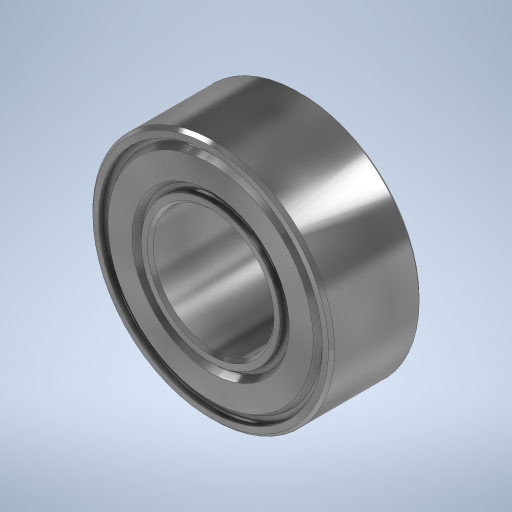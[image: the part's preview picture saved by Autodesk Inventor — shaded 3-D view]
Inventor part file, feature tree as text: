
AUTODESK INVENTOR PART (.ipt)
format: ipt  version: 2023.1 (Build 271208000, 208)  size: 379,392 bytes
history: native  units: mm
features: sketch x2, other x1, extrude x1, chamfer x1, revolve x1
ambient origin geometry x8: Origin, YZ Plane, XZ Plane, XY Plane, X Axis, Y Axis, Z Axis, Center Point
bodies: Body1 (feature_tree)
feature tree (6):
  other  "솔리드1"
  extrude  "돌출1"  Depth=4.0mm
  chamfer  "모따기1"  Distance=8.0mm
  revolve  "회전1"
  sketch  "스케치1"
  sketch  "스케치2"
